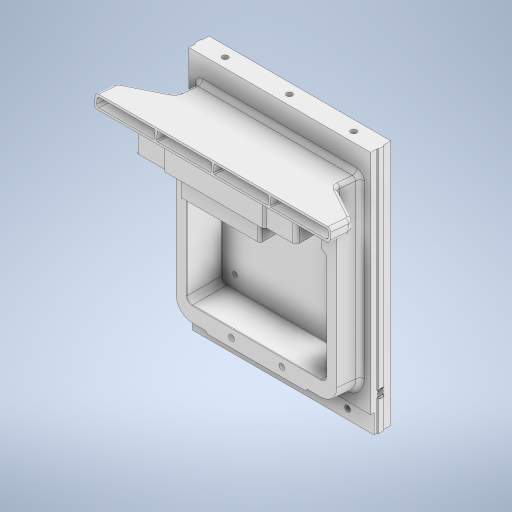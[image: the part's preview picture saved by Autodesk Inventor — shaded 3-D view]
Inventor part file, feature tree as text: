
AUTODESK INVENTOR PART (.ipt)
format: ipt  version: 2024 (Build 280153000, 153)  size: 3,045,888 bytes
history: native  units: mm
features: projected_geometry x46, sketch x41, extrude x39, fillet x39, plane x14, other x8, hole x6, chamfer x5, thicken_offset x5, mirror x3, split x1, loft x1, imported_body x1
ambient origin geometry x8: Origin, YZ Plane, XZ Plane, XY Plane, X Axis, Y Axis, Z Axis, Center Point
bodies: Solid2 (feature_tree)
feature tree (209):
  sketch  "Sketch2"  dims[d6=9.75mm d7=9.0mm]
  extrude  "Extrusion3"  Depth=9.0mm
  extrude  "Extrusion4"  Depth=12.0mm
  plane  "Work Plane1"
  extrude  "Extrusion5"  Depth=16.580628mm
  plane  "Work Plane2"
  extrude  "Extrusion6"  Depth=169.6mm TaperAngle=0.0deg
  extrude  "Extrusion7"  [1 undecoded]
  hole  "Hole1"  [1 undecoded]
  extrude  "Extrusion8"  TaperAngle=0.0deg  [1 undecoded]
  extrude  "Extrusion10"  Depth=10.0mm TaperAngle=0.0deg
  fillet  "Fillet3"  Radius=220.0mm
  fillet  "Fillet4"  [1 undecoded]
  fillet  "Fillet5"  Radius=27.0mm
  plane  "Work Plane3"
  sketch  "Sketch14"  dims[d23=32.5mm d24=10.0mm d25=0.0mm d26=220.0mm d27=120.0deg d28=27.0mm]
  extrude  "Extrusion11"  Depth=10.0mm TaperAngle=0.0deg
  extrude  "Extrusion12"  Depth=105.0mm
  fillet  "Fillet49"  Radius=38.0mm
  extrude  "Extrusion26"  Depth=10.0mm
  extrude  "Extrusion27"  Depth=15.0mm
  mirror  "Mirror1"
  fillet  "Fillet32"  Radius=3.0mm
  chamfer  "Chamfer4"  Distance=3.0mm
  sketch  "Sketch41"  dims[d123=30.0deg d124=80.0mm]
  plane  "Work Plane9"
  extrude  "Extrusion36"  Depth=15.0mm
  fillet  "Fillet41"  Radius=10.0mm
  chamfer  "Chamfer5"  Distance=10.0mm
  split  "Split1"
  thicken_offset  "Thicken1"
  fillet  "Fillet9"  Radius=5.0mm
  extrude  "Extrusion14"  Depth=35.0mm TaperAngle=0.0deg
  extrude  "Extrusion15"  Depth=5.0mm
  extrude  "Extrusion16"  Depth=5.0mm
  plane  "Work Plane14"
  fillet  "Fillet10"  [1 undecoded]
  fillet  "Fillet11"  [1 undecoded]
  fillet  "Fillet12"  Radius=20.0mm
  fillet  "Fillet13"  Radius=75.0mm
  fillet  "Fillet14"  Radius=10.0mm
  fillet  "Fillet15"  Radius=2.0mm
  plane  "Work Plane4"
  extrude  "Extrusion17"  Depth=10.0mm
  fillet  "Fillet16"  Radius=65.0mm
  fillet  "Fillet17"  Radius=10.0mm
  extrude  "Extrusion18"  Depth=10.0mm
  fillet  "Fillet18"  Radius=6.0mm
  extrude  "Extrusion22"  Depth=2.0mm
  fillet  "Fillet22"  Radius=2.0mm
  chamfer  "Chamfer2"  Distance=31.0mm
  extrude  "Extrusion23"  Depth=0.5mm
  fillet  "Fillet23"  Radius=95.0mm
  chamfer  "Chamfer3"  [1 undecoded]
  extrude  "Extrusion24"  Depth=80.0mm
  extrude  "Extrusion25"  TaperAngle=15.0deg  [1 undecoded]
  fillet  "Fillet24"  [1 undecoded]
  fillet  "Fillet25"  Radius=10.0mm
  fillet  "Fillet26"  Radius=8.0mm
  fillet  "Fillet27"  Radius=130.0mm
  extrude  "Extrusion28"  Depth=2.0mm
  plane  "Work Plane5"
  loft  "Loft1"
  fillet  "Fillet30"  Radius=8.5mm
  fillet  "Fillet31"  Radius=7.0mm
  sketch  "Sketch20"  dims[d59=0.0mm d60=0.0mm d61=15.0mm d62=3.0mm]
  thicken_offset  "Thicken2"
  thicken_offset  "Thicken3"
  thicken_offset  "Thicken4"
  sketch  "Sketch37"  dims[d115=1.0mm d116=2.0mm d117=0.5mm d118=95.0mm]
  extrude  "Extrusion31"  Depth=1.0mm TaperAngle=45.0deg
  extrude  "Extrusion32"  TaperAngle=120.0deg  [1 undecoded]
  fillet  "Fillet33"  Radius=15.0mm
  fillet  "Fillet34"  Radius=0.5mm
  fillet  "Fillet35"  Radius=75.0mm
  fillet  "Fillet38"  Radius=75.0mm
  fillet  "Fillet39"  Radius=2.0mm
  sketch  "Sketch39"  dims[d120=2.0mm d121=0.0mm d122=0.0mm]
  plane  "Work Plane6"
  plane  "Work Plane7"
  plane  "Work Plane8"
  extrude  "Extrusion33"  Depth=0.5mm
  extrude  "Extrusion34"  Depth=0.5mm
  hole  "Hole2"  [1 undecoded]
  fillet  "Fillet40"  Radius=50.0mm
  hole  "Hole3"  [1 undecoded]
  plane  "Work Plane10"
  extrude  "Extrusion37"  Depth=2.0mm TaperAngle=0.0deg
  plane  "Work Plane11"
  extrude  "Extrusion38"  Depth=2.0mm TaperAngle=0.0deg
  fillet  "Fillet42"  [1 undecoded]
  extrude  "Extrusion39"  TaperAngle=0.0deg  [1 undecoded]
  sketch  "Sketch46"  dims[d173=101.0mm d174=120.0deg d175=15.0mm d176=0.5mm d177=75.0mm d178=0.0mm d179=75.0mm d180=0.0mm d181=2.0mm]
  plane  "Work Plane12"
  extrude  "Extrusion40"  Depth=0.5mm
  mirror  "Mirror2"
  fillet  "Fillet43"  Radius=10.0mm
  fillet  "Fillet44"  Radius=2.0mm
  hole  "Hole4"  [1 undecoded]
  sketch  "Sketch48"  dims[d184=0.5mm d187=75.0mm]
  extrude  "Extrusion41"  Depth=53.0mm
  hole  "Hole5"  [1 undecoded]
  sketch  "Sketch52"  dims[d195=95.0mm d196=2.0mm d197=0.0mm]
  extrude  "Extrusion42"  Depth=53.0mm
  thicken_offset  "Thicken5"
  fillet  "Fillet45"  Radius=8.0mm
  fillet  "Fillet46"  Radius=12.0mm
  fillet  "Fillet47"  Radius=15.0mm
  fillet  "Fillet48"  Radius=18.0mm
  hole  "Hole6"  [1 undecoded]
  plane  "Work Plane13"
  extrude  "Extrusion43"  Depth=10.0mm TaperAngle=0.0deg
  extrude  "Extrusion44"  Depth=10.0mm TaperAngle=0.0deg
  chamfer  "Chamfer6"  Distance=10.0mm
  mirror  "Mirror3"
  fillet  "Fillet50"  Radius=2.0mm
  fillet  "Fillet51"  Radius=2.0mm
  sketch  "Sketch3"  dims[d8=30.0mm d9=12.0mm]
  sketch  "Sketch4"  dims[d10=45.0mm d11=16.580628mm]
  projected_geometry  "Projected Loop1"
  sketch  "Sketch5"  dims[d12=230.0mm d13=169.6mm d14=0.0mm]
  projected_geometry  "Projected Loop2"
  sketch  "Sketch6"  dims[d15=150.0mm d16=0.0mm d17=-8.0mm]
  projected_geometry  "Projected Loop3"
  sketch  "Sketch9"  dims[d18=130.0mm d19=130.0mm]
  projected_geometry  "Projected Loop4"
  sketch  "Sketch13"  dims[d20=25.0mm d21=0.0mm d22=0.0mm]
  projected_geometry  "Projected Loop6"
  other  "Srf1"
  sketch  "Sketch16"  dims[d29=20.0mm d30=10.0mm d31=0.0mm]
  other  "Srf2"
  sketch  "Sketch17"  dims[d32=105.0mm d33=105.0mm]
  projected_geometry  "Projected Loop8"
  sketch  "Sketch18"  dims[d34=4.4mm d35=6.0mm d36=4.0mm d37=2.0mm d38=90.0deg d39=1.5mm d40=0.0mm d41=38.0mm]
  projected_geometry  "Projected Loop9"
  sketch  "Sketch19"  dims[d42=10.0mm d43=0.0mm d58=178.0mm]
  projected_geometry  "Projected Loop10"
  projected_geometry  "Projected Loop11"
  projected_geometry  "Projected Loop12"
  sketch  "Sketch22"  dims[d63=6.0mm d65=3.0mm d66=2.0mm]
  sketch  "Sketch23"  dims[d67=2.0mm d68=15.0mm d69=10.0mm d70=0.0mm d71=10.0mm d72=0.0mm d78=5.0mm]
  sketch  "Sketch26"  dims[d79=180.0mm d80=35.0mm d81=0.0mm]
  sketch  "Sketch27"  dims[d83=0.4mm d84=5.0mm]
  sketch  "Sketch28"  dims[d85=4.5mm d86=5.0mm d87=120.0deg d88=120.0deg d89=20.0mm d90=75.0mm d91=10.0mm d92=0.0mm d93=2.0mm]
  sketch  "Sketch29"  dims[d94=2.0mm d95=2.0mm d96=65.0mm d97=10.0mm d98=0.0mm]
  projected_geometry  "Projected Loop16"
  projected_geometry  "Projected Loop17"
  projected_geometry  "Projected Loop18"
  sketch  "Sketch30"  dims[d99=10.0mm d100=0.0mm d101=2.0mm d102=6.0mm]
  sketch  "Sketch31"  dims[d103=6.0mm d104=2.0mm d105=2.0mm]
  sketch  "Sketch32"  dims[d106=1.0mm]
  sketch  "Sketch33"  dims[d111=101.0mm]
  sketch  "Sketch34"  dims[d112=101.0mm d113=31.0mm d114=0.0mm]
  other  "Srf4"
  other  "Srf5"
  other  "Srf6"
  projected_geometry  "Projected Loop22"
  projected_geometry  "Projected Loop23"
  projected_geometry  "Projected Loop24"
  sketch  "Sketch38"  dims[d119=95.0mm]
  projected_geometry  "Projected Loop25"
  projected_geometry  "Projected Loop26"
  projected_geometry  "Projected Loop27"
  sketch  "Sketch42"  dims[d125=3.0mm d126=15.0deg d127=15.0deg d128=10.0mm d157=8.0mm d158=130.0mm]
  projected_geometry  "Projected Loop28"
  sketch  "Sketch43"  dims[d159=5.5mm d160=0.0mm d161=2.0mm]
  sketch  "Sketch44"  dims[d162=0.5mm d163=2.0mm d164=45.0deg d165=8.5mm d166=8.5mm d167=7.0mm d168=0.0mm]
  sketch  "Sketch45"  dims[d169=1.5mm d170=1.0mm d171=2.0mm d172=45.0deg]
  projected_geometry  "Projected Loop29"
  sketch  "Sketch47"  dims[d182=0.5mm d183=0.5mm]
  sketch  "Sketch49"  dims[d188=135.0deg d189=85.0mm d192=50.0mm]
  sketch  "Sketch51"  dims[d193=5.0mm d194=16.0mm]
  projected_geometry  "Projected Loop30"
  projected_geometry  "Projected Loop31"
  other  "Srf7"
  sketch  "Sketch53"  dims[d198=2.0mm d199=0.0mm d201=2.0mm d202=0.0mm d204=-1.0mm]
  projected_geometry  "Projected Loop32"
  sketch  "Sketch54"  dims[d205=0.0mm d206=90.0deg d207=0.0mm d208=90.0deg]
  projected_geometry  "Projected Loop33"
  sketch  "Sketch55"  dims[d209=1.0mm d210=1.0mm d211=10.0mm d212=2.0mm d213=2.0mm d214=45.0deg d215=2.0mm d218=53.0mm d219=53.0mm d220=53.0mm d221=8.0mm d222=12.0mm d223=15.0mm d224=18.0mm d225=3.490659mm d226=10.0mm d227=0.0mm d228=10.0mm d229=0.0mm d230=10.0mm d231=0.0mm d232=2.0mm d233=2.0mm d234=2.0mm d238=3.0mm d239=1.0mm d240=1.0mm d243=8.0mm d246=8.0mm d247=0.0mm d248=8.0mm d249=0.0mm d250=1.0mm d251=0.5mm d252=8.25mm d253=60.0mm d254=60.0mm d255=-8.0mm d256=-7.0mm d257=3.0mm d258=10.0mm d259=0.0mm d260=10.0mm d261=0.0mm d262=5.4mm d263=6.0mm d264=4.0mm d265=2.0mm d266=90.0deg d267=12.0mm d268=0.0mm d269=1.0mm d270=2.0mm d271=16.0mm d272=16.0mm d273=6.0mm d277=30.0mm d278=30.0mm d279=0.0mm d280=1.0mm d281=2.0mm d282=2.0mm d283=45.0deg d284=5.4mm d285=6.0mm d286=4.0mm d287=2.0mm d288=90.0deg d289=8.0mm d290=0.0mm d291=-14.0mm d292=8.4mm d293=0.0mm d294=0.0mm d295=-20.0mm d296=0.5mm d297=0.5mm d298=0.0mm d299=0.0mm d300=0.5mm d301=18.0mm d302=3.25mm d303=0.0mm d304=2.0mm d305=2.0mm d306=2.0mm d307=16.75mm d308=23.0mm d309=-11.0mm d310=3.25mm d311=0.0mm d312=3.0mm d313=3.0mm d314=5.4mm d315=6.0mm d316=4.0mm d317=2.0mm d318=90.0deg d319=8.0mm d320=0.0mm d321=10.0mm d322=10.0mm d323=0.0mm d324=120.0mm d325=9.0mm d326=5.4mm d327=6.0mm d328=4.0mm d329=2.0mm d330=90.0deg d331=8.0mm d332=0.0mm d333=10.0mm d334=20.0mm d335=6.0mm d336=35.0mm d337=15.0mm d338=15.0mm d339=120.0deg d340=0.0mm d341=0.0mm d342=4.0mm d343=0.0mm d344=6.0mm d345=6.0mm d346=1.0mm d347=1.0mm d348=2.0mm d349=2.0mm d350=8.0mm d351=6.0mm d352=4.0mm d353=2.0mm d354=90.0deg d355=5.0mm d356=0.0mm d357=4.0mm d358=-8.0mm d359=8.25mm d360=4.0mm d361=0.0mm d362=5.5mm d363=6.0mm d364=1.0mm d365=0.0mm d366=1.0mm d367=2.0mm d368=45.0deg d369=0.5mm d370=0.5mm d73=0.0mm d74=0.0mm d75=0.0mm d76=0.0mm]
  other  "OffsetSrf1"
  extrude  "ExtrusionSrf1"  Depth=0.5mm
  extrude  "ExtrusionSrf2"  Depth=3.0mm
  extrude  "ExtrusionSrf3"  Depth=0.5mm
  extrude  "ExtrusionSrf4"  Depth=0.5mm
  extrude  "ExtrusionSrf5"  Depth=0.5mm
  projected_geometry  "Project Cut Edges1"
  projected_geometry  "Project Cut Edges2"
  projected_geometry  "Project Cut Edges3"
  projected_geometry  "Project Cut Edges4"
  projected_geometry  "Project Cut Edges5"
  projected_geometry  "Project Cut Edges6"
  imported_body  "Base"
  other  "Cap"
  projected_geometry  "Project Cut Edges7"
  projected_geometry  "Project Cut Edges8"
  projected_geometry  "Project Cut Edges9"
  projected_geometry  "Project Cut Edges11"
  projected_geometry  "Project Cut Edges12"
  projected_geometry  "Project Cut Edges13"
  projected_geometry  "Project Cut Edges14"
  projected_geometry  "Project Cut Edges16"
  projected_geometry  "Project Cut Edges17"
  projected_geometry  "Project Cut Edges18"
  projected_geometry  "Project Cut Edges19"
  projected_geometry  "Project Cut Edges20"
  projected_geometry  "Project Cut Edges21"
  projected_geometry  "Project Cut Edges22"
  projected_geometry  "Project Cut Edges23"
note: 17 required parameter values undecoded (feature->parameter linkage not recoverable at this tier; creation-order binding heuristic only, values carry confidence <= 0.55)
